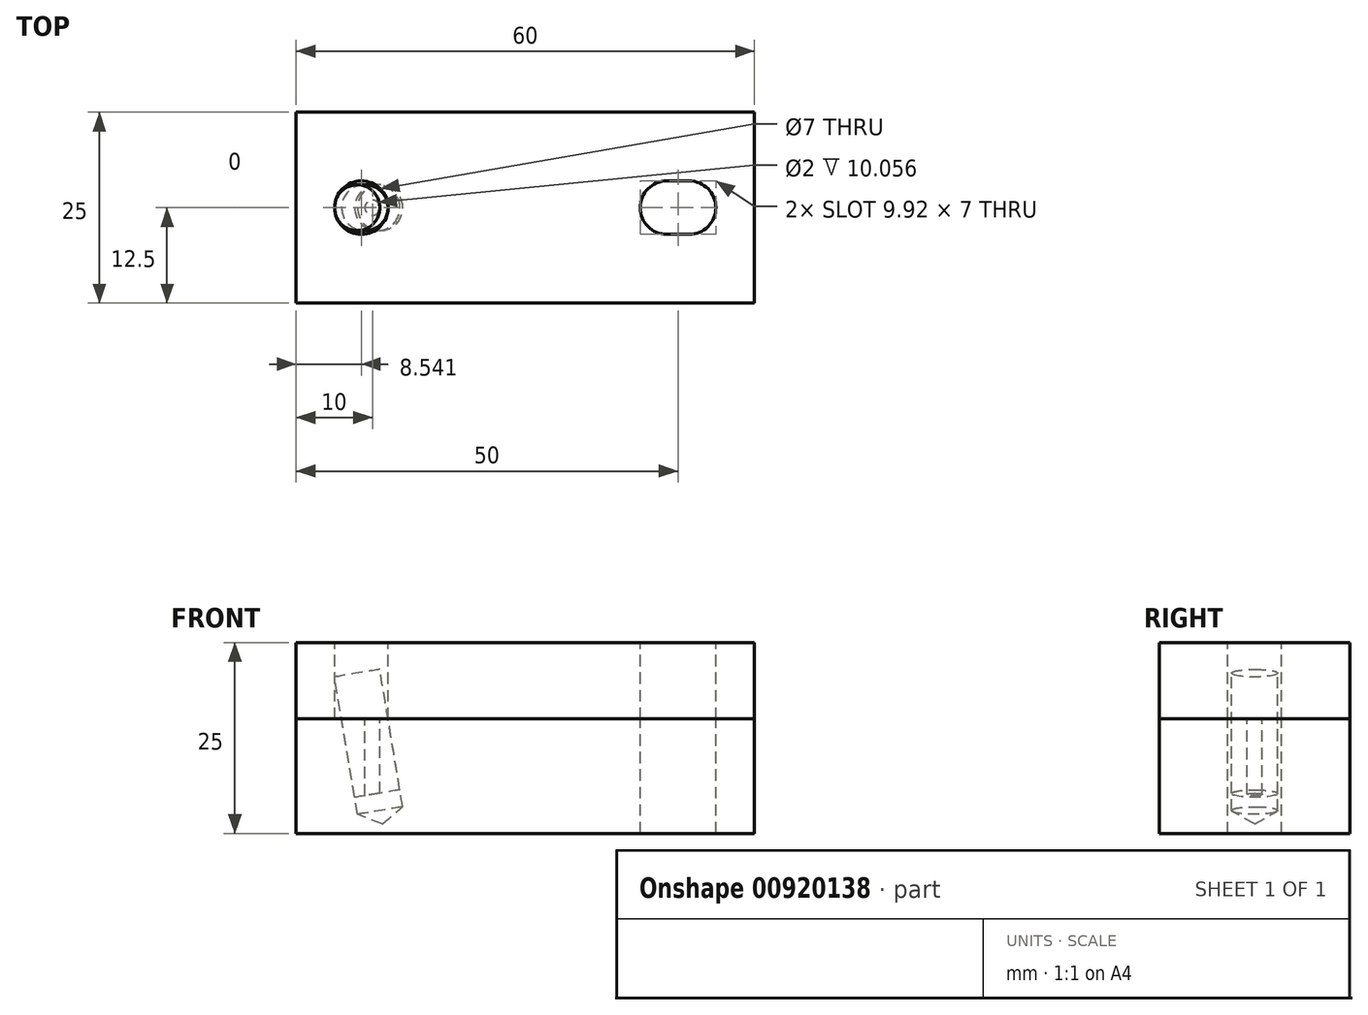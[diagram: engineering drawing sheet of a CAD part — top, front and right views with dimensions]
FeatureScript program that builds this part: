
annotation { "Feature Type Name" : "Feature", "Feature Type Description" : "" }
export const myFeature = defineFeature(function(context is Context, id is Id, definition is map)
    precondition{}
    {
        {
            var Q0;
            Q0=qCreatedBy(makeId("Front.planeOp"),FACE);
            var sketch = newSketch(context, id + "F0", { "sketchPlane" : qUnion([Q0])});
            skLineSegment(sketch, "E0.bottom", {"start": v(-30, 0) * mm, "end": v(30, 0) * mm});
            skLineSegment(sketch, "E0.top", {"start": v(-30, -15) * mm, "end": v(30, -15) * mm});
            skLineSegment(sketch, "E0.left", {"start": v(-30, 0) * mm, "end": v(-30, -15) * mm});
            skLineSegment(sketch, "E0.right", {"start": v(30, 0) * mm, "end": v(30, -15) * mm});
            skSolve(sketch);
        }
        {
            var Q0;
            Q0 = qSketchRegion(id + "F0", true);
            extrude(context, id + "F1", {"entities" : qUnion([Q0]), "endBound" : BoundingType.SYMMETRIC, "depth" : 25 * mm, "offsetDistance" : 25 * mm});
        }
        {
            var Q0;
            Q0=qCreatedBy(makeId("Front.planeOp"),FACE);
            var sketch = newSketch(context, id + "F2", { "sketchPlane" : qUnion([Q0])});
            skLineSegment(sketch, "E1.bottom", {"start": v(-21, 0) * mm, "end": v(-19, 0) * mm, "construction": true});
            skLineSegment(sketch, "E1.top", {"start": v(-21, -12) * mm, "end": v(-19, -12) * mm, "construction": true});
            skLineSegment(sketch, "E1.left", {"start": v(-21, 0) * mm, "end": v(-21, -12) * mm, "construction": true});
            skLineSegment(sketch, "E1.right", {"start": v(-19, 0) * mm, "end": v(-19, -12) * mm, "construction": true});
            skLineSegment(sketch, "E2.bottom", {"start": v(-20, 0) * mm, "end": v(-20, 0) * mm});
            skLineSegment(sketch, "E2.top", {"start": v(-20, -12) * mm, "end": v(-20, -12) * mm});
            skLineSegment(sketch, "E2.left", {"start": v(-20, 0) * mm, "end": v(-20, -12) * mm, "construction": true});
            skLineSegment(sketch, "E2.right", {"start": v(-20, 0) * mm, "end": v(-20, -12) * mm, "construction": true});
            skLineSegment(sketch, "E3", {"start": v(-18.7, -13.78) * mm, "end": v(-22, 6) * mm});
            skLineSegment(sketch, "E4", {"start": v(-22, 6) * mm, "end": v(-24.96, 5.5) * mm});
            skLineSegment(sketch, "E5", {"start": v(-24.96, 5.5) * mm, "end": v(-21.96, -12.5) * mm});
            skLineSegment(sketch, "E6", {"start": v(-21.96, -12.5) * mm, "end": v(-18.7, -13.78) * mm});
            skLineSegment(sketch, "E7", {"start": v(-21.96, -12.5) * mm, "end": v(-19, -12) * mm, "construction": true});
            skSolve(sketch);
        }
        {
            var Q0;
            Q0=makeQuery(id+"F2.imprint","IMPRINT",FACE,{"disambiguationData":[TD([[makeQuery(id+"F2.imprint","IMPRINT",EDGE,{"derivedFrom":sQuery(id+"F2.wireOp",EDGE,"E3")}),1.0]])]});
            var Q1;
            Q1=sQuery(id+"F2.wireOp",EDGE,"E3");
            revolve(context, id + "F3", {"operationType" : NewBodyOperationType.REMOVE, "surfaceOperationType" : NewSurfaceOperationType.NEW, "entities" : qUnion([Q0]), "axis" : qUnion([Q1]), "revolveType" : RevolveType.FULL, "oppositeDirection" : true});
        }
        {
            var Q0;
            Q0=qCreatedBy(makeId("Front.planeOp"),FACE);
            var sketch = newSketch(context, id + "F4", { "sketchPlane" : qUnion([Q0])});
            skLineSegment(sketch, "E8.bottom", {"start": v(-21, 0) * mm, "end": v(-20, 0) * mm});
            skLineSegment(sketch, "E8.top", {"start": v(-21, -12) * mm, "end": v(-20, -12) * mm});
            skLineSegment(sketch, "E8.left", {"start": v(-21, 0) * mm, "end": v(-21, -12) * mm});
            skLineSegment(sketch, "E8.right", {"start": v(-20, 0) * mm, "end": v(-20, -12) * mm});
            skSolve(sketch);
        }
        {
            var Q0;
            Q0 = qSketchRegion(id + "F4", true);
            var Q1;
            Q1=sQuery(id+"F4.wireOp",EDGE,"E8.right");
            revolve(context, id + "F5", {"surfaceOperationType" : NewSurfaceOperationType.NEW, "entities" : qUnion([Q0]), "axis" : qUnion([Q1]), "revolveType" : RevolveType.FULL});
        }
        {
            var Q0;
            Q0=qCreatedBy(makeId("Front.planeOp"),FACE);
            var sketch = newSketch(context, id + "F6", { "sketchPlane" : qUnion([Q0])});
            skLineSegment(sketch, "E9.bottom", {"start": v(-30, 0) * mm, "end": v(30, 0) * mm});
            skLineSegment(sketch, "E9.top", {"start": v(-30, 10) * mm, "end": v(30, 10) * mm});
            skLineSegment(sketch, "E9.left", {"start": v(-30, 0) * mm, "end": v(-30, 10) * mm});
            skLineSegment(sketch, "E9.right", {"start": v(30, 0) * mm, "end": v(30, 10) * mm});
            skSolve(sketch);
        }
        {
            var Q0;
            Q0 = qSketchRegion(id + "F6", true);
            extrude(context, id + "F7", {"entities" : qUnion([Q0]), "endBound" : BoundingType.SYMMETRIC, "depth" : 25 * mm, "offsetDistance" : 25 * mm});
        }
        {
            var Q0;
            Q0=qCreatedBy(makeId("Front.planeOp"),FACE);
            var sketch = newSketch(context, id + "F8", { "sketchPlane" : qUnion([Q0])});
            skLineSegment(sketch, "E10.top", {"start": v(-21.46, 10) * mm, "end": v(-24.96, 10) * mm});
            skLineSegment(sketch, "E10.left", {"start": v(-21.46, 0) * mm, "end": v(-21.46, 10) * mm});
            skLineSegment(sketch, "E10.right", {"start": v(-24.96, 0) * mm, "end": v(-24.96, 10) * mm});
            skLineSegment(sketch, "E11.0", {"start": v(-22, 6) * mm, "end": v(-24.96, 5.5) * mm, "construction": true});
            skLineSegment(sketch, "E12", {"start": v(-22, 6) * mm, "end": v(-19.04, 6.5) * mm, "construction": true});
            skLineSegment(sketch, "E13", {"start": v(-19.04, 6.5) * mm, "end": v(-17.96, 0) * mm, "construction": true});
            skLineSegment(sketch, "E14", {"start": v(-21.46, 0) * mm, "end": v(-24.96, 0) * mm});
            skLineSegment(sketch, "E15", {"start": v(-21.46, 0) * mm, "end": v(-17.96, 0) * mm, "construction": true});
            skSolve(sketch);
        }
        {
            var Q0;
            Q0 = qSketchRegion(id + "F8", true);
            var Q1;
            Q1=sQuery(id+"F8.wireOp",EDGE,"E10.left");
            revolve(context, id + "F9", {"operationType" : NewBodyOperationType.REMOVE, "surfaceOperationType" : NewSurfaceOperationType.NEW, "entities" : qUnion([Q0]), "axis" : qUnion([Q1]), "revolveType" : RevolveType.FULL, "oppositeDirection" : true});
        }
        {
            var Q0;
            Q0=makeQuery(id+"F7.opExtrude","SWEPT_FACE",FACE,{"disambiguationData":[OSD([sQuery(id+"F6.wireOp",EDGE,"E9.top")])]});
            var sketch = newSketch(context, id + "F10", { "sketchPlane" : qUnion([Q0])});
            skArc(sketch, "E16", {"start": v(18.54, 3.5) * mm, "mid": v(15.04, 0) * mm, "end": v(18.54, -3.5) * mm});
            skArc(sketch, "E17", {"start": v(21.46, -3.5) * mm, "mid": v(24.96, 0) * mm, "end": v(21.46, 3.5) * mm});
            skCircle(sketch, "E18.0", {"center": v(-21.46, 0) * mm, "radius": 3.5 * mm, "construction": true});
            skLineSegment(sketch, "E19", {"start": v(-21.46, 0) * mm, "end": v(-24.96, 0) * mm, "construction": true});
            skLineSegment(sketch, "E20", {"start": v(21.46, 3.5) * mm, "end": v(18.54, 3.5) * mm});
            skLineSegment(sketch, "E21", {"start": v(18.54, -3.5) * mm, "end": v(21.46, -3.5) * mm});
            skLineSegment(sketch, "E22", {"start": v(18.54, 0) * mm, "end": v(21.46, 0) * mm, "construction": true});
            skLineSegment(sketch, "E23", {"start": v(0, 0) * mm, "end": v(20, 0) * mm, "construction": true});
            skLineSegment(sketch, "E24", {"start": v(0, 0) * mm, "end": v(24.96, 0) * mm, "construction": true});
            skLineSegment(sketch, "E25", {"start": v(0, 0) * mm, "end": v(-24.96, 0) * mm});
            skSolve(sketch);
        }
        {
            var Q0;
            Q0 = qSketchRegion(id + "F10", true);
            extrude(context, id + "F11", {"entities" : qUnion([Q0]), "operationType" : NewBodyOperationType.REMOVE, "oppositeDirection" : true, "depth" : 25 * mm, "offsetDistance" : 25 * mm});
        }
        {
            var Q0;
            Q0=qCreatedBy(makeId("Front.planeOp"),FACE);
            var sketch = newSketch(context, id + "F12", { "sketchPlane" : qUnion([Q0])});
            skLineSegment(sketch, "E26", {"start": v(-22.33, -10.28) * mm, "end": v(-24.96, 5.5) * mm});
            skLineSegment(sketch, "E27", {"start": v(-24.96, 5.5) * mm, "end": v(-22, 6) * mm});
            skLineSegment(sketch, "E28", {"start": v(-22, 6) * mm, "end": v(-19.37, -9.78) * mm});
            skLineSegment(sketch, "E29", {"start": v(-19.37, -9.78) * mm, "end": v(-22.33, -10.28) * mm});
            skSolve(sketch);
        }
        {
            var Q0;
            Q0=makeQuery(id+"F12.imprint","IMPRINT",FACE,{"disambiguationData":[TD([[makeQuery(id+"F12.imprint","IMPRINT",EDGE,{"derivedFrom":sQuery(id+"F12.wireOp",EDGE,"E26")}),-1.0]])]});
            var Q1;
            Q1=sQuery(id+"F12.wireOp",EDGE,"E28");
            revolve(context, id + "F13", {"surfaceOperationType" : NewSurfaceOperationType.NEW, "entities" : qUnion([Q0]), "axis" : qUnion([Q1]), "revolveType" : RevolveType.FULL});
        }
        {
            var Q0;
            Q0=qCreatedBy(makeId("Front.planeOp"),FACE);
            var sketch = newSketch(context, id + "F14", { "sketchPlane" : qUnion([Q0])});
            skLineSegment(sketch, "E30.bottom", {"start": v(-21, -12) * mm, "end": v(-20, -12) * mm});
            skLineSegment(sketch, "E30.top", {"start": v(-21, 0) * mm, "end": v(-20, 0) * mm});
            skLineSegment(sketch, "E30.left", {"start": v(-21, -12) * mm, "end": v(-21, 0) * mm});
            skLineSegment(sketch, "E31", {"start": v(-20, -12) * mm, "end": v(-20, 0) * mm});
            skPoint(sketch, "E32.orphan", {"position": v(-19, -12) * mm});
            skSolve(sketch);
        }
        {
            var Q0;
            Q0 = qSketchRegion(id + "F14", true);
            var Q1;
            Q1=sQuery(id+"F14.wireOp",EDGE,"E31");
            revolve(context, id + "F15", {"operationType" : NewBodyOperationType.REMOVE, "surfaceOperationType" : NewSurfaceOperationType.NEW, "entities" : qUnion([Q0]), "axis" : qUnion([Q1]), "revolveType" : RevolveType.FULL, "oppositeDirection" : true});
        }
    });
